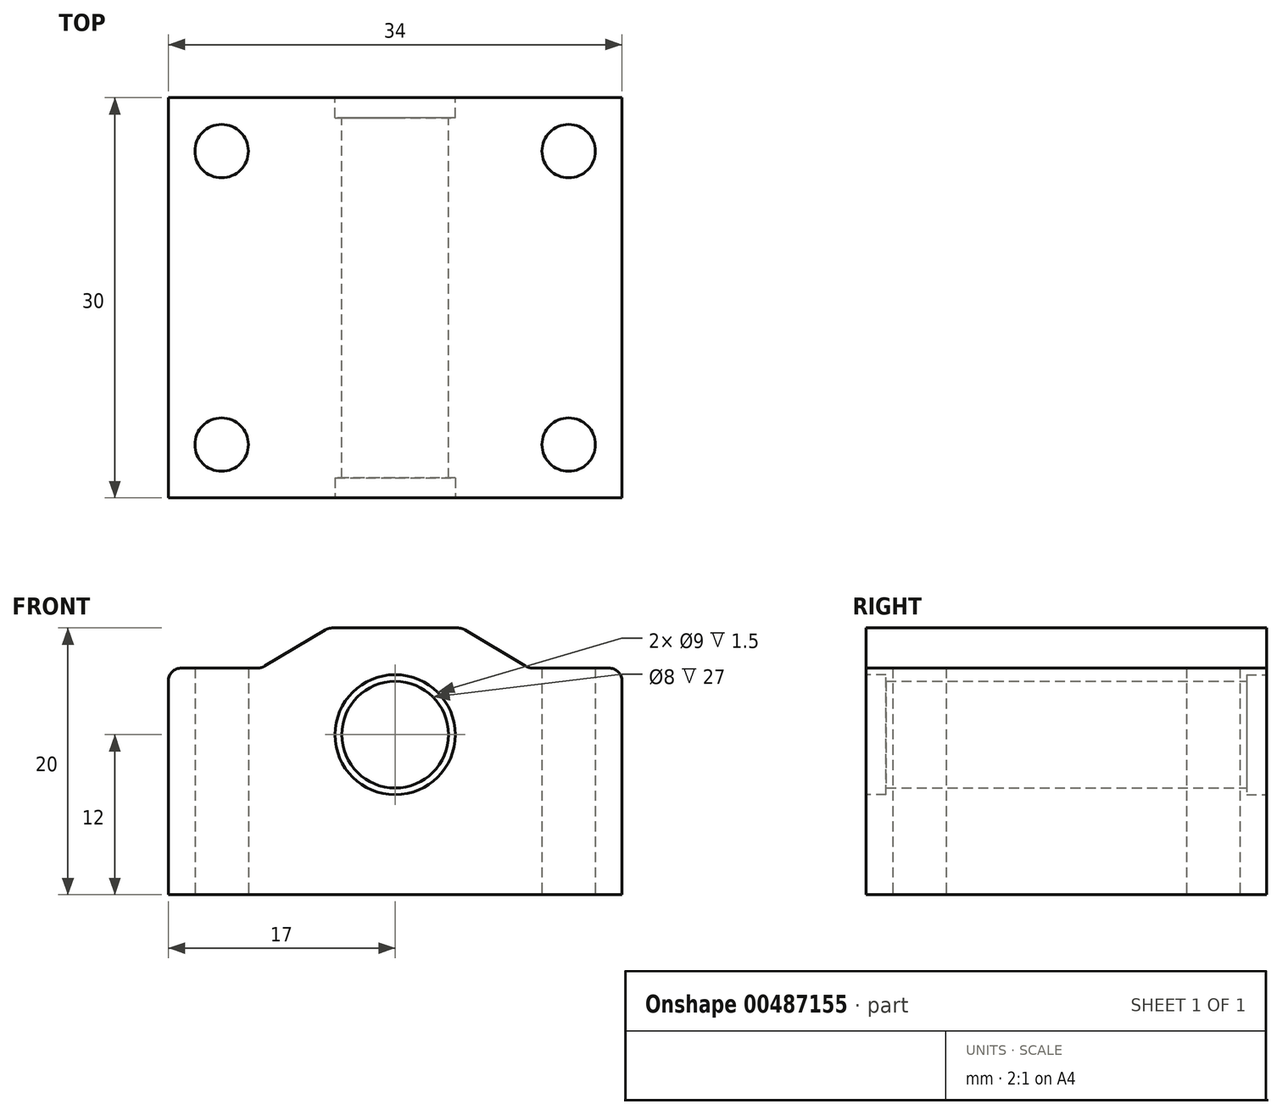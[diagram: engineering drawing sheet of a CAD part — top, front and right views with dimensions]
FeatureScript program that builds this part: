
annotation { "Feature Type Name" : "Feature", "Feature Type Description" : "" }
export const myFeature = defineFeature(function(context is Context, id is Id, definition is map)
    precondition{}
    {
        {
            var Q0;
            Q0=qCreatedBy(makeId("Front.planeOp"),FACE);
            var sketch = newSketch(context, id + "F0", { "sketchPlane" : qUnion([Q0])});
            skCircle(sketch, "E0", {"center": v(0, 0) * mm, "radius": 4 * mm});
            skLineSegment(sketch, "E1.bottom", {"start": v(-17, 5) * mm, "end": v(-10, 5) * mm});
            skLineSegment(sketch, "E1.top", {"start": v(-17, -12) * mm, "end": v(17, -12) * mm});
            skLineSegment(sketch, "E1.left", {"start": v(-17, 5) * mm, "end": v(-17, -12) * mm});
            skLineSegment(sketch, "E1.right", {"start": v(17, 5) * mm, "end": v(17, -12) * mm});
            skCircle(sketch, "E2", {"center": v(0, 0) * mm, "radius": 4.5 * mm, "construction": true});
            skArc(sketch, "E3", {"start": v(6.24, 5) * mm, "mid": v(0, 8) * mm, "end": v(-6.24, 5) * mm, "construction": true});
            skLineSegment(sketch, "E4.trimOffspring", {"start": v(10, 5) * mm, "end": v(17, 5) * mm});
            skLineSegment(sketch, "E5", {"start": v(-5, 8) * mm, "end": v(5, 8) * mm});
            skLineSegment(sketch, "E6", {"start": v(5, 8) * mm, "end": v(10, 5) * mm});
            skLineSegment(sketch, "E7", {"start": v(-5, 8) * mm, "end": v(-10, 5) * mm});
            skSolve(sketch);
        }
        {
            var Q0;
            Q0 = qSketchRegion(id + "F0", true);
            extrude(context, id + "F1", {"entities" : qUnion([Q0]), "depth" : 30 * mm});
        }
        {
            var Q0;
            Q0=makeQuery(id+"F1.opExtrude","SWEPT_FACE",FACE,{"disambiguationData":[OSD([sQuery(id+"F0.wireOp",EDGE,"E1.top")])]});
            var sketch = newSketch(context, id + "F2", { "sketchPlane" : qUnion([Q0])});
            skCircle(sketch, "E8", {"center": v(-13, 26) * mm, "radius": 2 * mm});
            skCircle(sketch, "E9", {"center": v(-13, 4) * mm, "radius": 2 * mm});
            skCircle(sketch, "E10", {"center": v(13, 26) * mm, "radius": 2 * mm});
            skCircle(sketch, "E11", {"center": v(13, 4) * mm, "radius": 2 * mm});
            skSolve(sketch);
        }
        {
            var Q0;
            Q0 = qSketchRegion(id + "F2", true);
            extrude(context, id + "F3", {"entities" : qUnion([Q0]), "operationType" : NewBodyOperationType.REMOVE, "oppositeDirection" : true, "depth" : 25 * mm});
        }
        {
            var Q0;
            Q0=makeQuery(id+"F1.opExtrude","CAP_FACE",FACE,{"disambiguationData":[OSD([sQuery(id+"F0.wireOp",EDGE,"E0"),sQuery(id+"F0.wireOp",EDGE,"E1.bottom"),sQuery(id+"F0.wireOp",EDGE,"E1.top"),sQuery(id+"F0.wireOp",EDGE,"E1.left"),sQuery(id+"F0.wireOp",EDGE,"E1.right"),sQuery(id+"F0.wireOp",EDGE,"E4.trimOffspring"),sQuery(id+"F0.wireOp",EDGE,"E5"),sQuery(id+"F0.wireOp",EDGE,"E6"),sQuery(id+"F0.wireOp",EDGE,"E7")])],"isStart":false});
            var sketch = newSketch(context, id + "F4", { "sketchPlane" : qUnion([Q0])});
            skCircle(sketch, "E12", {"center": v(0, 0) * mm, "radius": 4.5 * mm});
            skSolve(sketch);
        }
        {
            var Q0;
            Q0 = qSketchRegion(id + "F4", true);
            extrude(context, id + "F5", {"entities" : qUnion([Q0]), "operationType" : NewBodyOperationType.REMOVE, "oppositeDirection" : true, "depth" : 1.5 * mm});
        }
        {
            var Q0;
            Q0=makeQuery(id+"F1.opExtrude","CAP_FACE",FACE,{"disambiguationData":[OSD([sQuery(id+"F0.wireOp",EDGE,"E0"),sQuery(id+"F0.wireOp",EDGE,"E1.bottom"),sQuery(id+"F0.wireOp",EDGE,"E1.top"),sQuery(id+"F0.wireOp",EDGE,"E1.left"),sQuery(id+"F0.wireOp",EDGE,"E1.right"),sQuery(id+"F0.wireOp",EDGE,"E4.trimOffspring"),sQuery(id+"F0.wireOp",EDGE,"E5"),sQuery(id+"F0.wireOp",EDGE,"E6"),sQuery(id+"F0.wireOp",EDGE,"E7")])],"isStart":true});
            var sketch = newSketch(context, id + "F6", { "sketchPlane" : qUnion([Q0])});
            skCircle(sketch, "E13", {"center": v(0, 0) * mm, "radius": 4.5 * mm});
            skSolve(sketch);
        }
        {
            var Q0;
            Q0 = qSketchRegion(id + "F6", true);
            extrude(context, id + "F7", {"entities" : qUnion([Q0]), "operationType" : NewBodyOperationType.REMOVE, "oppositeDirection" : true, "depth" : 1.5 * mm});
        }
        {
            var Q0;
            Q0=makeQuery(id+"F1.opExtrude","SWEPT_EDGE",EDGE,{"disambiguationData":[OSD([sQuery(id+"F0.wireOp",EDGE,"E1.bottom"),sQuery(id+"F0.wireOp",EDGE,"E1.left")])]});
            var Q1;
            Q1=makeQuery(id+"F1.opExtrude","SWEPT_EDGE",EDGE,{"disambiguationData":[OSD([sQuery(id+"F0.wireOp",EDGE,"E1.bottom"),sQuery(id+"F0.wireOp",EDGE,"E7")])]});
            var Q2;
            Q2=makeQuery(id+"F1.opExtrude","SWEPT_EDGE",EDGE,{"disambiguationData":[OSD([sQuery(id+"F0.wireOp",EDGE,"E5"),sQuery(id+"F0.wireOp",EDGE,"E7")])]});
            var Q3;
            Q3=makeQuery(id+"F1.opExtrude","SWEPT_EDGE",EDGE,{"disambiguationData":[OSD([sQuery(id+"F0.wireOp",EDGE,"E5"),sQuery(id+"F0.wireOp",EDGE,"E6")])]});
            var Q4;
            Q4=makeQuery(id+"F1.opExtrude","SWEPT_EDGE",EDGE,{"disambiguationData":[OSD([sQuery(id+"F0.wireOp",EDGE,"E4.trimOffspring"),sQuery(id+"F0.wireOp",EDGE,"E6")])]});
            var Q5;
            Q5=makeQuery(id+"F1.opExtrude","SWEPT_EDGE",EDGE,{"disambiguationData":[OSD([sQuery(id+"F0.wireOp",EDGE,"E1.right"),sQuery(id+"F0.wireOp",EDGE,"E4.trimOffspring")])]});
            fillet(context, id + "F8", {"entities" : qUnion([Q0, Q1, Q2, Q3, Q4, Q5]), "radius" : 1 * mm, "tangentPropagation" : true, "allowEdgeOverflow" : false});
        }
    });
